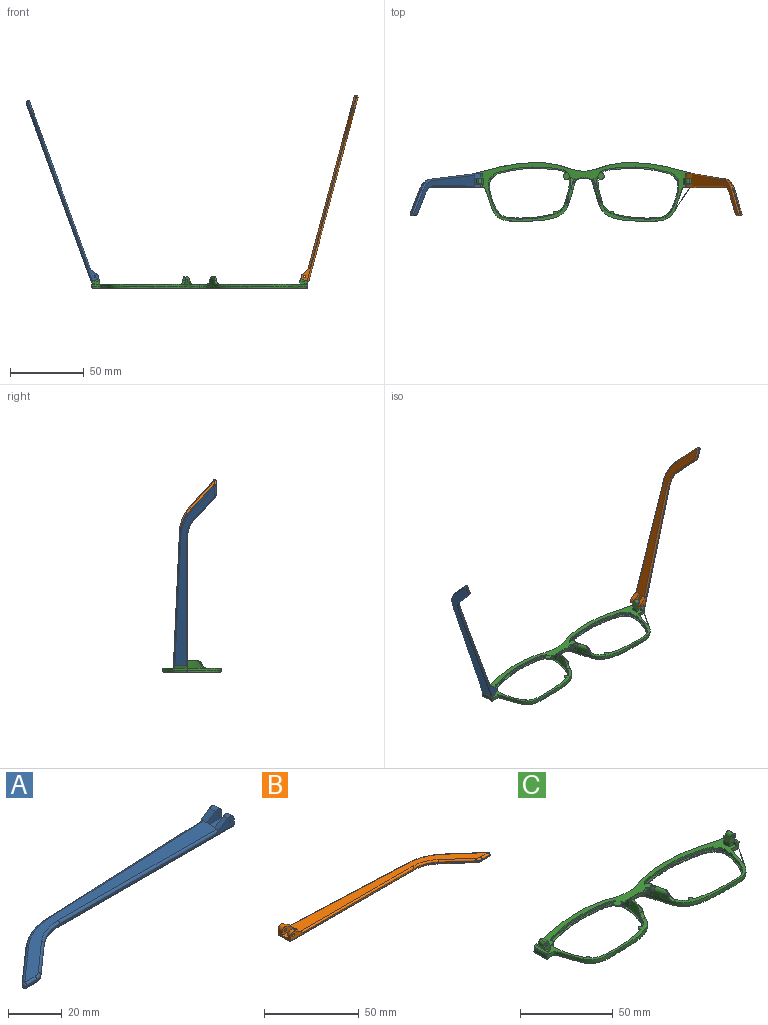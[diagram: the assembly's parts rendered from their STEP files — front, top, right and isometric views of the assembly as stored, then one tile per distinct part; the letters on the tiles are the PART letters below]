
ASSEMBLY  parts=3 mates=2
PART A: 43 faces, bbox 130.2x29.5x5.9 mm
  f0: plane 9.62x3.72mm, normal (1,0,0), area 24.7mm2, adj f1,f3,f4,f5,f10,f16,f18,f28
  f1: cylinder r=2.2mm len=3.45mm, axis (0,-1,0), area 11mm2, adj f0,f2,f4,f37
  f2: plane 6.01x3.91mm, normal (-0.55,0,0.84), area 12.7mm2, adj f1,f4,f9,f19,f37
  f3: plane 2.26x0.1mm, normal (0,0,1), area 0.1mm2, adj f0,f5,f18
  f4: plane 92.1x4.9mm, normal (0,-1,0), area 79.9mm2, adj f0,f1,f2,f14,f19,f36,f42
  f5: plane 93.42x4.13mm, normal (-0.04,1,0), area 64.8mm2, adj f0,f3,f11,f15,f17,f27,f28
  f6: plane 17.82x15.72mm, normal (-0.66,0.75,0), area 14.3mm2, adj f11,f12,f25,f30
  f7: plane 5.46x0.6mm, normal (0,-1,0), area 3.3mm2, adj f12,f13,f23,f32
  f8: plane 14.99x13.23mm, normal (0.66,-0.75,0), area 12mm2, adj f13,f14,f21,f34
  f9: plane 121.18x26.73mm, normal (0,0,1), area 627.7mm2, adj f2,f17,f19,f20,f21,f22,f23,f25
  f10: plane 129.1x27.08mm, normal (0,0,-1), area 686.5mm2, adj f0,f28,f29,f30,f32,f33,f34,f35
  f11: cylinder r=30mm len=18.52mm, axis (0,0,-1), area 12.2mm2, adj f5,f6,f26,f29
  f12: cylinder r=1mm len=1.75mm, axis (0,0,-1), area 1.5mm2, adj f6,f7,f24,f31
  f13: cylinder r=5mm len=3.31mm, axis (0,0,-1), area 2.2mm2, adj f7,f8,f22,f33
  f14: cylinder r=20mm len=13.23mm, axis (0,0,1), area 8.7mm2, adj f4,f8,f20,f35
  f15: plane 5.66x0.25mm, normal (0,0,-1), area 0.7mm2, adj f5,f17,f18
  f16: cylinder r=2.2mm len=3.45mm, axis (0,-1,0), area 14.8mm2, adj f0,f17,f18,f38
  f17: plane 6.01x3.91mm, normal (-0.55,0,0.84), area 16.9mm2, adj f5,f9,f15,f16,f18,f27,f38
  f18: plane 7.92x3.3mm, normal (0,1,0), area 15.9mm2, adj f0,f3,f15,f16,f17,f41
  f19: cylinder r=1mm len=84.18mm, axis (-1,0,0), area 131.4mm2, adj f2,f4,f9,f20
  f20: torus R=21mm, axis (0,0,1), area 23.1mm2, adj f9,f14,f19,f21
  f21: cylinder r=1mm len=15.65mm, axis (-0.75,-0.66,0), area 31.4mm2, adj f8,f9,f20,f22
  f22: torus R=4mm, axis (0,0,1), area 5.3mm2, adj f9,f13,f21,f23
  f23: cylinder r=1mm len=5.46mm, axis (-1,0,0), area 8.6mm2, adj f7,f9,f22,f24
  f24: sphere r=1mm, area 2.4mm2, adj f12,f23,f25
  f25: cylinder r=1mm len=18.48mm, axis (0.75,0.66,0), area 37.3mm2, adj f6,f9,f24,f26
  f26: torus R=29mm, axis (0,0,1), area 31.6mm2, adj f9,f11,f25,f27
  f27: cylinder r=1mm len=85.5mm, axis (1,0.04,0), area 133.5mm2, adj f5,f9,f17,f26
  f28: cylinder r=1mm len=93.46mm, axis (-1,-0.04,0), area 146.9mm2, adj f0,f5,f10,f29
  f29: torus R=29mm, axis (0,0,1), area 31.6mm2, adj f10,f11,f28,f30
  f30: cylinder r=1mm len=18.48mm, axis (-0.75,-0.66,0), area 37.3mm2, adj f6,f10,f29,f31
  f31: sphere r=1mm, area 2.4mm2, adj f12,f30,f32
  f32: cylinder r=1mm len=5.46mm, axis (1,0,0), area 8.6mm2, adj f7,f10,f31,f33
  f33: torus R=4mm, axis (0,0,1), area 5.3mm2, adj f10,f13,f32,f34
  f34: cylinder r=1mm len=15.65mm, axis (0.75,0.66,0), area 31.4mm2, adj f8,f10,f33,f35
  f35: torus R=21mm, axis (0,0,1), area 23.1mm2, adj f10,f14,f34,f36
  f36: cylinder r=1mm len=92.1mm, axis (1,0,0), area 144.7mm2, adj f0,f4,f10,f35
  f37: plane 7.92x4.7mm, normal (0,1,0), area 27mm2, adj f0,f1,f2,f39,f40,f42
  f38: plane 7.92x4.7mm, normal (0,-1,0), area 27mm2, adj f0,f16,f17,f39,f40,f41
  f39: plane 7.92x4.1mm, normal (0,0,1), area 32.5mm2, adj f0,f37,f38,f40
  f40: plane 4.1x1.4mm, normal (1,0,0), area 5.7mm2, adj f9,f37,f38,f39
  f41: cylinder r=0.5mm len=3.1mm, axis (0,-1,0), area 9.7mm2, adj f18,f38
  f42: cylinder r=0.5mm len=2.3mm, axis (0,-1,0), area 7.2mm2, adj f4,f37
PART B: 43 faces, bbox 130.2x29.5x5.9 mm
  f0: plane 9.62x3.72mm, normal (-1,0,0), area 24.7mm2, adj f1,f3,f4,f5,f10,f16,f18,f28
  f1: cylinder r=2.2mm len=3.45mm, axis (0,-1,0), area 11mm2, adj f0,f2,f4,f37
  f2: plane 6.01x3.91mm, normal (0.55,0,0.84), area 12.7mm2, adj f1,f4,f9,f19,f37
  f3: plane 2.26x0.1mm, normal (0,0,1), area 0.1mm2, adj f0,f5,f18
  f4: plane 92.1x4.9mm, normal (0,-1,0), area 78.2mm2, adj f0,f1,f2,f14,f19,f36,f42
  f5: plane 93.42x4.13mm, normal (0.04,1,0), area 64.8mm2, adj f0,f3,f11,f15,f17,f27,f28
  f6: plane 17.82x15.72mm, normal (0.66,0.75,0), area 14.3mm2, adj f11,f12,f25,f30
  f7: plane 5.46x0.6mm, normal (0,-1,0), area 3.3mm2, adj f12,f13,f23,f32
  f8: plane 14.99x13.23mm, normal (-0.66,-0.75,0), area 12mm2, adj f13,f14,f21,f34
  f9: plane 121.18x26.73mm, normal (0,0,1), area 627.7mm2, adj f2,f17,f19,f20,f21,f22,f23,f25
  f10: plane 129.1x27.08mm, normal (0,0,-1), area 686.5mm2, adj f0,f28,f29,f30,f32,f33,f34,f35
  f11: cylinder r=30mm len=18.52mm, axis (0,0,-1), area 12.2mm2, adj f5,f6,f26,f29
  f12: cylinder r=1mm len=1.75mm, axis (0,0,-1), area 1.5mm2, adj f6,f7,f24,f31
  f13: cylinder r=5mm len=3.31mm, axis (0,0,-1), area 2.2mm2, adj f7,f8,f22,f33
  f14: cylinder r=20mm len=13.23mm, axis (0,0,1), area 8.7mm2, adj f4,f8,f20,f35
  f15: plane 5.66x0.25mm, normal (0,0,-1), area 0.7mm2, adj f5,f17,f18
  f16: cylinder r=2.2mm len=3.45mm, axis (0,-1,0), area 14.8mm2, adj f0,f17,f18,f38
  f17: plane 6.01x3.91mm, normal (0.55,0,0.84), area 16.9mm2, adj f5,f9,f15,f16,f18,f27,f38
  f18: plane 7.92x3.3mm, normal (0,1,0), area 14.3mm2, adj f0,f3,f15,f16,f17,f41
  f19: cylinder r=1mm len=84.18mm, axis (1,0,0), area 131.4mm2, adj f2,f4,f9,f20
  f20: torus R=21mm, axis (0,0,1), area 23.1mm2, adj f9,f14,f19,f21
  f21: cylinder r=1mm len=15.65mm, axis (0.75,-0.66,0), area 31.4mm2, adj f8,f9,f20,f22
  f22: torus R=4mm, axis (0,0,1), area 5.3mm2, adj f9,f13,f21,f23
  f23: cylinder r=1mm len=5.46mm, axis (1,0,0), area 8.6mm2, adj f7,f9,f22,f24
  f24: sphere r=1mm, area 2.4mm2, adj f12,f23,f25
  f25: cylinder r=1mm len=18.48mm, axis (-0.75,0.66,0), area 37.3mm2, adj f6,f9,f24,f26
  f26: torus R=29mm, axis (0,0,1), area 31.6mm2, adj f9,f11,f25,f27
  f27: cylinder r=1mm len=85.5mm, axis (-1,0.04,0), area 133.5mm2, adj f5,f9,f17,f26
  f28: cylinder r=1mm len=93.46mm, axis (1,-0.04,0), area 146.9mm2, adj f0,f5,f10,f29
  f29: torus R=29mm, axis (0,0,1), area 31.6mm2, adj f10,f11,f28,f30
  f30: cylinder r=1mm len=18.48mm, axis (0.75,-0.66,0), area 37.3mm2, adj f6,f10,f29,f31
  f31: sphere r=1mm, area 2.4mm2, adj f12,f30,f32
  f32: cylinder r=1mm len=5.46mm, axis (-1,0,0), area 8.6mm2, adj f7,f10,f31,f33
  f33: torus R=4mm, axis (0,0,1), area 5.3mm2, adj f10,f13,f32,f34
  f34: cylinder r=1mm len=15.65mm, axis (-0.75,0.66,0), area 31.4mm2, adj f8,f10,f33,f35
  f35: torus R=21mm, axis (0,0,1), area 23.1mm2, adj f10,f14,f34,f36
  f36: cylinder r=1mm len=92.1mm, axis (-1,0,0), area 144.7mm2, adj f0,f4,f10,f35
  f37: plane 7.92x4.7mm, normal (0,1,0), area 25.4mm2, adj f0,f1,f2,f39,f40,f42
  f38: plane 7.92x4.7mm, normal (0,-1,0), area 25.4mm2, adj f0,f16,f17,f39,f40,f41
  f39: plane 7.92x4.1mm, normal (0,0,1), area 32.5mm2, adj f0,f37,f38,f40
  f40: plane 4.1x1.4mm, normal (-1,0,0), area 5.7mm2, adj f9,f37,f38,f39
  f41: cylinder r=0.88mm len=3.1mm, axis (0,-1,0), area 17mm2, adj f18,f38
  f42: cylinder r=0.88mm len=2.3mm, axis (0,-1,0), area 12.6mm2, adj f4,f37
PART C: 118 faces, bbox 148.1x40.9x10.4 mm
  f0: bspline ~1.82x1.22mm, area 0.7mm2, adj f1,f114,f116,f117
  f1: bspline ~2.66x2.04mm, area 1.9mm2, adj f0,f2,f113,f114,f117
  f2: bspline ~3.55x3.47mm, area 3.7mm2, adj f1,f3,f112,f113,f117
  f3: plane 147.39x40.2mm, normal (0,0,1), area 882.5mm2, adj f2,f4,f16,f17,f18,f19,f20,f21
  f4: plane 1.23x0.04mm, normal (0,0,1), area 0mm2, adj f3,f5,f114
  f5: plane 2.76x2.53mm, normal (0,-1,0), area 3.9mm2, adj f4,f6,f15,f16,f24
  f6: plane 9.65x1.24mm, normal (0,0,1), area 8.2mm2, adj f5,f7,f14,f15,f19,f20,f21,f24
  f7: plane 5.77x5.06mm, normal (0,-1,0), area 17mm2, adj f6,f8,f9,f11,f12,f13,f14,f23
  f8: cylinder r=1.98mm len=4mm, axis (0,-1,0), area 12.4mm2, adj f7,f12,f14,f21
  f9: plane 4x3.31mm, normal (-0.94,0,0.34), area 14.1mm2, adj f7,f10,f11,f21
  f10: plane 4x0.02mm, normal (0.34,0,0.94), area 0.1mm2, adj f9,f21,f22
  f11: cylinder r=1.98mm len=4mm, axis (0,1,0), area 12.4mm2, adj f7,f9,f12,f21
  f12: plane 4x0.01mm, normal (0.34,0,0.94), area 0mm2, adj f7,f8,f11,f21
  f13: cylinder r=0.88mm len=4mm, axis (0,-1,0), area 22mm2, adj f7,f21
  f14: plane 4x2.21mm, normal (0.94,0,-0.34), area 9.4mm2, adj f6,f7,f8,f21
  f15: plane 9.71x1.44mm, normal (0.34,0,0.94), area 13.9mm2, adj f5,f6,f16,f17,f18,f19
  f16: cone r=1mm half-angle=20deg, axis (0,0,1), area 2.3mm2, adj f3,f5,f15,f17
  f17: plane 7.67x1.6mm, normal (0.94,0,-0.34), area 13mm2, adj f3,f15,f16,f18
  f18: cylinder r=1mm len=2.28mm, axis (-0.34,0,-0.94), area 3mm2, adj f3,f15,f17,f19
  f19: plane 2.1x1.69mm, normal (0,1,0), area 2.8mm2, adj f3,f6,f15,f18,f20
  f20: plane 3.3x2.1mm, normal (-1,0,0), area 6.9mm2, adj f3,f6,f19,f21
  f21: plane 6.97x5.07mm, normal (0,1,0), area 22.7mm2, adj f3,f6,f8,f9,f10,f11,f12,f13
  f22: plane 4x2.36mm, normal (-1,0,0), area 9.5mm2, adj f3,f10,f21,f23
  f23: plane 3.2x2.36mm, normal (0,-1,0), area 5.7mm2, adj f3,f7,f22,f24
  f24: plane 2.35x2.1mm, normal (-1,0,0), area 4.9mm2, adj f3,f5,f6,f7,f23
  f25: bspline ~3.7x3.66mm, area 7.8mm2, adj f3,f26,f31,f41,f114
  f26: bspline ~7.26x7.26mm, area 6.3mm2, adj f25,f27,f31,f41
  f27: bspline ~10.28x4.83mm, area 21.4mm2, adj f26,f28,f31,f41,f114,f117
  f28: plane 3.63x0.97mm, normal (0,0,1), area 0.3mm2, adj f27,f29,f41
  f29: bspline ~8.14x4.16mm, area 6.4mm2, adj f28,f30,f41,f112,f117
  f30: extruded ~4.98x1.37mm, area 6.6mm2, adj f29,f41
  f31: extruded ~4.44x3.32mm, area 15.1mm2, adj f25,f26,f27,f32,f114
  f32: plane 4.46x1.45mm, normal (0,0,1), area 0.1mm2, adj f31,f114
  f33: cylinder r=1.3mm len=2.6mm, axis (0,0,1), area 2.7mm2, adj f3,f34,f41
  f34: plane 2.61x2.29mm, normal (0,0,-1), area 4.2mm2, adj f33,f41
  f35: cylinder r=1.3mm len=1.93mm, axis (0,0,1), area 1.5mm2, adj f3,f36,f41
  f36: plane 1.95x1.68mm, normal (0,0,-1), area 1.5mm2, adj f35,f41
  f37: cylinder r=2.28mm len=3.13mm, axis (0,0,1), area 2.5mm2, adj f3,f38,f41
  f38: plane 3.14x2.79mm, normal (0,0,-1), area 3.9mm2, adj f37,f41
  f39: cylinder r=2.28mm len=4.55mm, axis (0,0,1), area 5.5mm2, adj f3,f40,f41
  f40: plane 4.55x4.51mm, normal (0,0,-1), area 15.4mm2, adj f39,f41
  f41: extruded ~55.69x35.36mm, area 226.5mm2, adj f3,f25,f26,f27,f28,f29,f30,f33
  f42: extruded ~55.69x35.36mm, area 160.5mm2, adj f41,f43
  f43: plane 56.06x35.45mm, normal (0,0,1), area 127mm2, adj f42,f44
  f44: bspline ~56.23x35.9mm, area 235.3mm2, adj f43,f45
  f45: plane 144.78x37.84mm, normal (0,0,-1), area 578.9mm2, adj f44,f46,f49,f52,f53,f54,f55,f57
  f46: bspline ~56.22x35.9mm, area 235.3mm2, adj f45,f47
  f47: plane 56.06x35.45mm, normal (0,0,1), area 127mm2, adj f46,f48
  f48: extruded ~55.69x35.36mm, area 160.5mm2, adj f47,f86
  f49: bspline ~8.97x1.23mm, area 12.6mm2, adj f45,f50,f51,f114
  f50: bspline ~1x1mm, area 0.8mm2, adj f49,f60,f114
  f51: bspline ~1.04x1mm, area 0.7mm2, adj f49,f52,f114
  f52: bspline ~45.77x8.55mm, area 59.8mm2, adj f45,f51,f53,f114
  f53: bspline ~37.01x6.7mm, area 56.6mm2, adj f45,f52,f54,f111
  f54: bspline ~37.01x6.7mm, area 56.6mm2, adj f45,f53,f55,f110
  f55: bspline ~45.77x8.55mm, area 59.8mm2, adj f45,f54,f56,f109
  f56: bspline ~1.04x1mm, area 0.8mm2, adj f55,f57,f109
  f57: bspline ~8.97x1.23mm, area 12.6mm2, adj f45,f56,f58,f109
  f58: bspline ~1x1mm, area 0.8mm2, adj f57,f59,f109
  f59: bspline ~73.42x30.37mm, area 161.7mm2, adj f45,f58,f60,f109
  f60: bspline ~73.42x30.37mm, area 161.7mm2, adj f45,f50,f59,f114
  f61: bspline ~6.38x2.14mm, area 2.6mm2, adj f3,f62,f113,f114
  f62: bspline ~6.38x2.14mm, area 2.6mm2, adj f3,f61,f63,f109
  f63: bspline ~2.1x1.46mm, area 0.6mm2, adj f62,f64,f76,f109
  f64: bspline ~2.65x2.03mm, area 1.9mm2, adj f63,f65,f68,f76,f109
  f65: bspline ~2.19x1.4mm, area 0.7mm2, adj f64,f66,f68,f109
  f66: extruded ~3.67x3.11mm, area 5.9mm2, adj f65,f67,f68,f109
  f67: bspline ~5.24x1.75mm, area 0mm2, adj f66,f109
  f68: bspline ~6.1x4.93mm, area 12.6mm2, adj f64,f65,f66,f69,f74,f76,f109
  f69: bspline ~10.28x4.83mm, area 21.5mm2, adj f68,f70,f71,f73,f86,f109
  f70: plane 3.63x0.97mm, normal (0,0,1), area 0.3mm2, adj f69,f74,f86
  f71: extruded ~4.44x3.32mm, area 15.1mm2, adj f69,f72,f73,f87,f109
  f72: plane 4.46x1.45mm, normal (0,0,1), area 0.1mm2, adj f71,f109
  f73: bspline ~7.26x7.26mm, area 6.2mm2, adj f69,f71,f86,f87
  f74: bspline ~8.14x4.16mm, area 6.4mm2, adj f68,f70,f75,f77,f86
  f75: extruded ~4.98x1.36mm, area 6.6mm2, adj f74,f86
  f76: bspline ~3.55x3.47mm, area 3.7mm2, adj f3,f63,f64,f68,f77
  f77: bspline ~5.57x4.33mm, area 7.6mm2, adj f3,f74,f76,f86
  f78: cylinder r=2.28mm len=4.55mm, axis (0,0,1), area 5.5mm2, adj f3,f79,f86
  f79: plane 4.55x4.51mm, normal (0,0,-1), area 15.4mm2, adj f78,f86
  f80: cylinder r=2.28mm len=3.13mm, axis (0,0,1), area 2.5mm2, adj f3,f81,f86
  f81: plane 3.14x2.79mm, normal (0,0,-1), area 3.9mm2, adj f80,f86
  f82: cylinder r=1.3mm len=1.93mm, axis (0,0,1), area 1.5mm2, adj f3,f83,f86
  f83: plane 1.95x1.68mm, normal (0,0,-1), area 1.5mm2, adj f82,f86
  f84: cylinder r=1.3mm len=2.6mm, axis (0,0,1), area 2.7mm2, adj f3,f85,f86
  f85: plane 2.61x2.29mm, normal (0,0,-1), area 4.2mm2, adj f84,f86
  f86: extruded ~55.69x35.36mm, area 226.5mm2, adj f3,f48,f69,f70,f73,f74,f75,f77
  f87: bspline ~3.7x3.66mm, area 7.8mm2, adj f3,f71,f73,f86,f109
  f88: plane 2.35x2.1mm, normal (1,0,0), area 4.9mm2, adj f3,f89,f91,f98,f100
  f89: plane 2.76x2.53mm, normal (0,-1,0), area 3.9mm2, adj f88,f90,f91,f107,f108
  f90: plane 9.71x1.44mm, normal (-0.34,0,0.94), area 13.9mm2, adj f89,f91,f104,f105,f106,f107
  f91: plane 9.65x1.24mm, normal (0,0,1), area 8.2mm2, adj f88,f89,f90,f92,f98,f102,f103,f104
  f92: plane 4x2.21mm, normal (-0.94,0,-0.34), area 9.4mm2, adj f91,f93,f98,f102
  f93: cylinder r=1.98mm len=4mm, axis (0,-1,0), area 12.4mm2, adj f92,f94,f98,f102
  f94: plane 4x0.01mm, normal (-0.34,0,0.94), area 0mm2, adj f93,f95,f98,f102
  f95: cylinder r=1.98mm len=4mm, axis (0,1,0), area 12.4mm2, adj f94,f96,f98,f102
  f96: plane 4x3.31mm, normal (0.94,0,0.34), area 14.1mm2, adj f95,f97,f98,f102
  f97: plane 4x0.02mm, normal (-0.34,0,0.94), area 0.1mm2, adj f96,f101,f102
  f98: plane 5.77x5.06mm, normal (0,-1,0), area 17mm2, adj f88,f91,f92,f93,f94,f95,f96,f99
  f99: cylinder r=0.88mm len=4mm, axis (0,-1,0), area 22mm2, adj f98,f102
  f100: plane 3.2x2.36mm, normal (0,-1,0), area 5.7mm2, adj f3,f88,f98,f101
  f101: plane 4x2.36mm, normal (1,0,0), area 9.5mm2, adj f3,f97,f100,f102
  f102: plane 6.97x5.07mm, normal (0,1,0), area 22.7mm2, adj f3,f91,f92,f93,f94,f95,f96,f97
  f103: plane 3.3x2.1mm, normal (1,0,0), area 6.9mm2, adj f3,f91,f102,f104
  f104: plane 2.1x1.69mm, normal (0,1,0), area 2.8mm2, adj f3,f90,f91,f103,f105
  f105: cylinder r=1mm len=2.28mm, axis (0.34,0,-0.94), area 3mm2, adj f3,f90,f104,f106
  f106: plane 7.67x1.6mm, normal (-0.94,0,-0.34), area 13mm2, adj f3,f90,f105,f107
  f107: cone r=1mm half-angle=20deg, axis (0,0,1), area 2.3mm2, adj f3,f89,f90,f106
  f108: plane 1.23x0.04mm, normal (0,0,1), area 0mm2, adj f3,f89,f109
  f109: extruded ~73.26x39.83mm, area 293.6mm2, adj f3,f55,f56,f57,f58,f59,f62,f63
  f110: extruded ~35.39x5.69mm, area 72.2mm2, adj f3,f54,f109,f111
  f111: extruded ~35.39x5.69mm, area 72.2mm2, adj f3,f53,f110,f114
  f112: bspline ~5.71x4.38mm, area 7.6mm2, adj f2,f3,f29,f41
  f113: bspline ~2.1x1.46mm, area 0.6mm2, adj f1,f2,f61,f114
  f114: extruded ~73.26x39.83mm, area 293.6mm2, adj f0,f1,f3,f4,f25,f27,f31,f32
  f115: bspline ~5.24x1.75mm, area 0mm2, adj f114,f116
  f116: extruded ~3.67x3.11mm, area 5.9mm2, adj f0,f114,f115,f117
  f117: bspline ~6.1x4.93mm, area 12.7mm2, adj f0,f1,f2,f27,f29,f114,f116
PLACE A rot(axis=(0,1,0),70deg) t=(-84.77,-5.75,56)mm
PLACE B rot(axis=(0,-1,0),75deg) t=(68.2,-5.75,-61.61)mm
PLACE C t=(10.15,-1.13,-5.77)mm
MATE revolute A.f1 <-> C.f95  axis (0,-1,0) through (-60.89,2.72,1.22)mm
MATE revolute B.f41 <-> C.f8  axis (0,-1,0) through (81.2,2.72,1.21)mm
